# Revit family: Q-SYS NC-12x80 & 20x60
name_source: partatom
category: Communication Devices
revit_build: Autodesk Revit 2018 (Build: 20190510_1515(x64)
units: mm (PartAtom-declared; Revit-internal decimal feet)

## family parameters
Cut with Voids When Loaded = No
Host = Face
Maintain Annotation Orientation = No
Part Type = Normal
Room Calculation Point = No
Round Connector Dimension = Use Diameter
Shared = No

## types (2) — shared parameters
Current Draw (A) = 1
Default Elevation = 1219 mm
Depth = 169 mm  [stored 0.554462 ft]
Description = Q-SYS Networked PTZ Camera
Height = 197 mm
Lens Type = Integrated
Manufacturer = QSC, LLC
Manufacturer URL = www.qsc.com
Motorized Zoom = Yes
Product Documentation Link = https://www.qsc.com
Product Page URL = https://www.qsc.com
URL = https://www.qsc.com
Voltage DC = 12 VDC or PoE Type 1, Class 3
Weight (kg) = 1.6
Weight (lb) = 3.5
Width = 153 mm  [stored 0.501969 ft]

## per-type parameters (varying)
| type | Camera Type | Focal Length | Lens Zoom Max |
| NC-12x80 | Q-SYS PTZ with Max H FOV 80° | 3.47-41.65mm | 12 |
| NC-20x60 | Q-SYS PTZ with Max H FOV 60° | 6.25-125mm | 20 |

note: column(s) folded — value = type name in every type: Model

note: [stored X ft] marks values corroborated as IEEE doubles in the binary element streams (Revit-internal decimal feet)

## geometry (parser evidence)
native form markers: Sweep x14
no freeform markers — native parametric forms only
